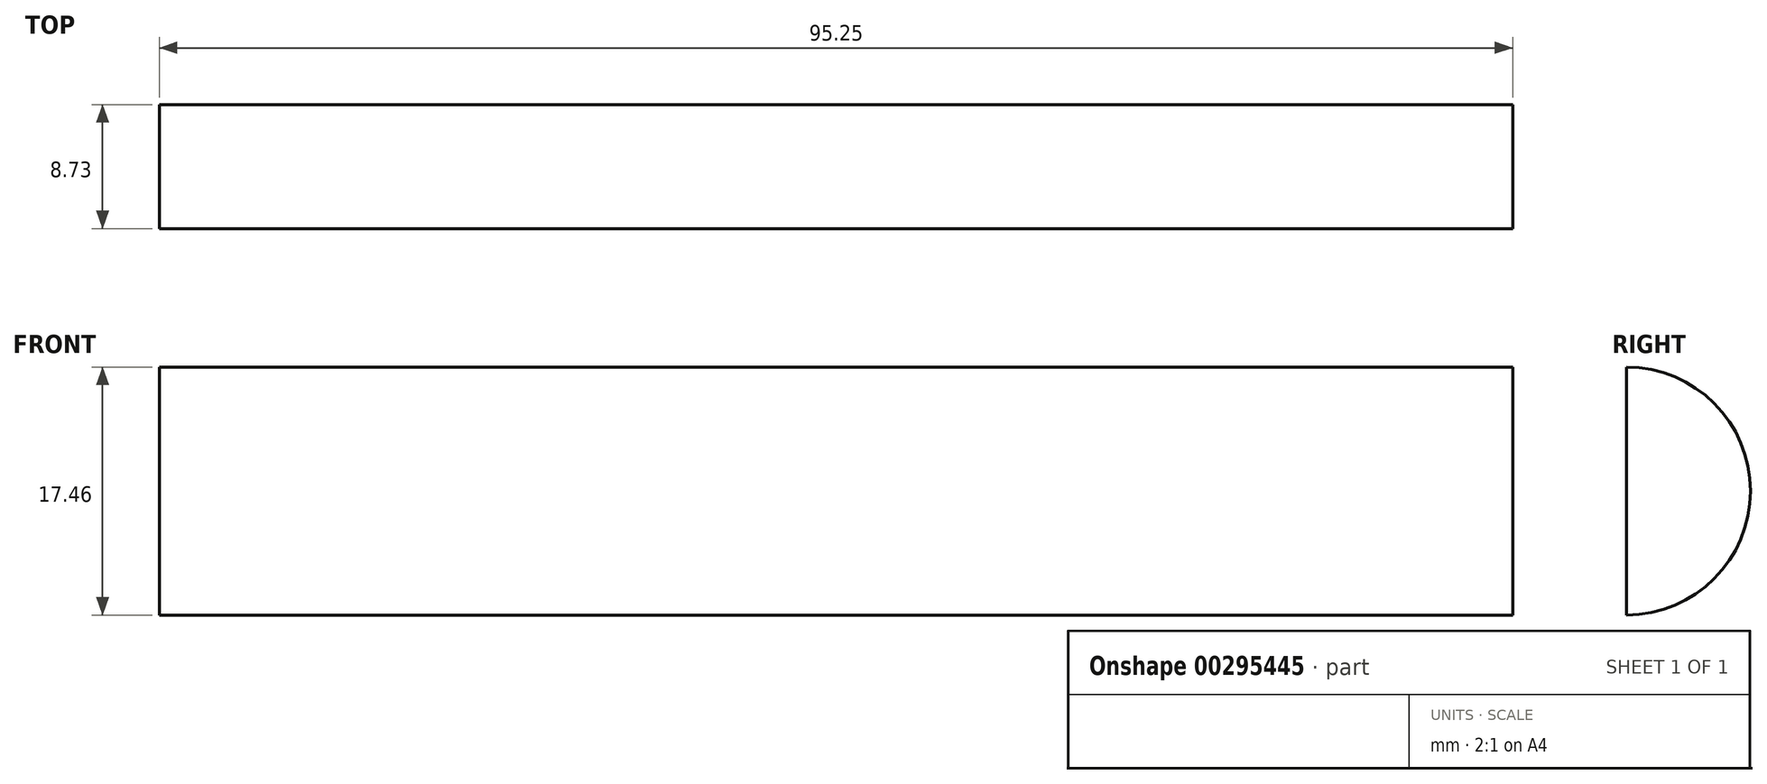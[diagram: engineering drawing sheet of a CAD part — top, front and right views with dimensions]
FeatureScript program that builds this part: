
annotation { "Feature Type Name" : "Feature", "Feature Type Description" : "" }
export const myFeature = defineFeature(function(context is Context, id is Id, definition is map)
    precondition{}
    {
        {
            var Q0;
            Q0=qCreatedBy(makeId("Right.planeOp"),FACE);
            var sketch = newSketch(context, id + "F0", { "sketchPlane" : qUnion([Q0])});
            skArc(sketch, "E0", {"start": v(0, -8.73) * mm, "mid": v(8.73, 0) * mm, "end": v(0, 8.73) * mm});
            skLineSegment(sketch, "E1", {"start": v(0, 8.73) * mm, "end": v(0, -8.73) * mm});
            skSolve(sketch);
        }
        {
            var Q0;
            Q0 = qSketchRegion(id + "F0", true);
            extrude(context, id + "F1", {"entities" : qUnion([Q0]), "depth" : 95.25 * mm});
        }
    });
